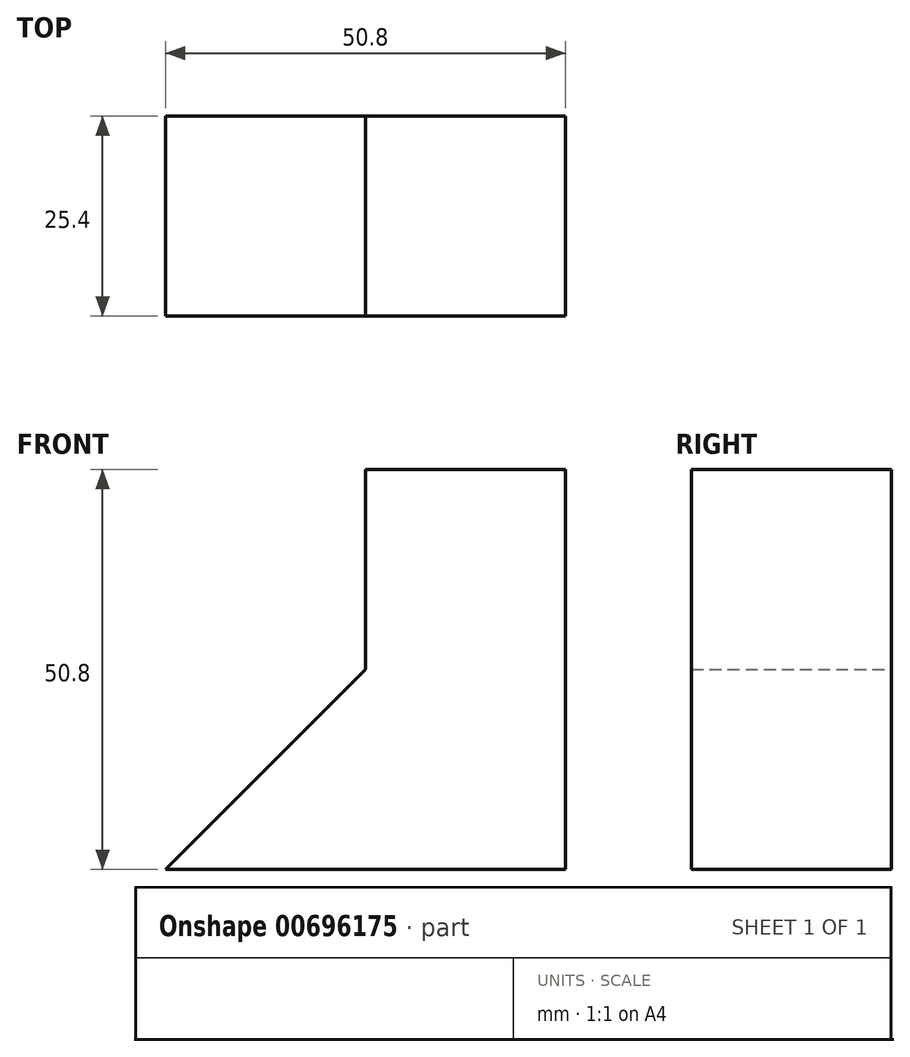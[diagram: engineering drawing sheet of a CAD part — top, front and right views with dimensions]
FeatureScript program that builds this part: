
annotation { "Feature Type Name" : "Feature", "Feature Type Description" : "" }
export const myFeature = defineFeature(function(context is Context, id is Id, definition is map)
    precondition{}
    {
        {
            var Q0;
            Q0=qCreatedBy(makeId("Front.planeOp"),FACE);
            var sketch = newSketch(context, id + "F0", { "sketchPlane" : qUnion([Q0])});
            skLineSegment(sketch, "E0", {"start": v(-36.95, 28.74) * mm, "end": v(-36.95, 54.14) * mm});
            skLineSegment(sketch, "E1", {"start": v(-36.95, 54.14) * mm, "end": v(-11.55, 54.14) * mm});
            skLineSegment(sketch, "E2", {"start": v(-11.55, 54.14) * mm, "end": v(-11.55, 3.34) * mm});
            skLineSegment(sketch, "E3", {"start": v(-11.55, 3.34) * mm, "end": v(-62.35, 3.34) * mm});
            skLineSegment(sketch, "E4", {"start": v(-62.35, 3.34) * mm, "end": v(-36.95, 28.74) * mm});
            skSolve(sketch);
        }
        {
            var Q0;
            Q0=makeQuery(id+"F0.imprint","IMPRINT",FACE,{"disambiguationData":[TD([[makeQuery(id+"F0.imprint","IMPRINT",EDGE,{"derivedFrom":sQuery(id+"F0.wireOp",EDGE,"E0")}),-1.0]])]});
            extrude(context, id + "F1", {"entities" : qUnion([Q0]), "depth" : 25.4 * mm, "offsetDistance" : 25.4 * mm});
        }
    });
